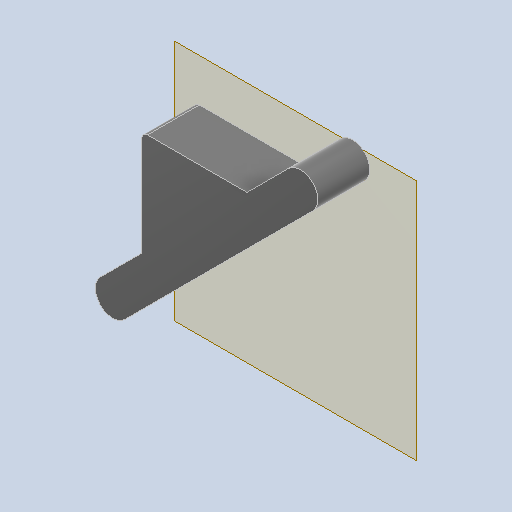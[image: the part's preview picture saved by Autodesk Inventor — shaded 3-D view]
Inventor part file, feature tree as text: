
AUTODESK INVENTOR PART (.ipt)
format: ipt  version: 2023 (Build 270158000, 158)  size: 305,664 bytes
history: native  units: in
note: dims shown in document units (in); Inventor stores cm internally (conversion verified against a paired STEP export)
features: reference x10, extrude x2, sketch x2, other x2, plane x1, fillet x1
ambient origin geometry x8: Origin, YZ Plane, XZ Plane, XY Plane, X Axis, Y Axis, Z Axis, Center Point
bodies: Solid1 (feature_tree), Body_Normal_2 (feature_tree)
feature tree (18):
  plane  "Work Plane1"
  extrude  "Extrusion1"  Depth=0.4724in
  extrude  "Extrusion2"  Depth=0.7087in
  fillet  "Fillet1"  Radius=0.0787in
  sketch  "Sketch1"  dims[d0=0.4724in d1=0.4724in]
  reference  "Reference1"
  reference  "Reference2"
  reference  "Reference3"
  reference  "Reference4"
  reference  "Reference5"
  reference  "Reference6"
  reference  "Reference7"
  reference  "Reference8"
  reference  "Reference9"
  reference  "Reference10"
  sketch  "Sketch2"  dims[d2=1.7717in d3=1.7717in d4=0.0787in d5=0.7087in d6=0.0in d7=1.5748in d9=360.0deg d11=0.315in d12=0.0in d13=0.315in]
  other  "<userpath>\Downloads\frame\parts\Reader\RF622A.iam"
  other  "RF622A.iam"
